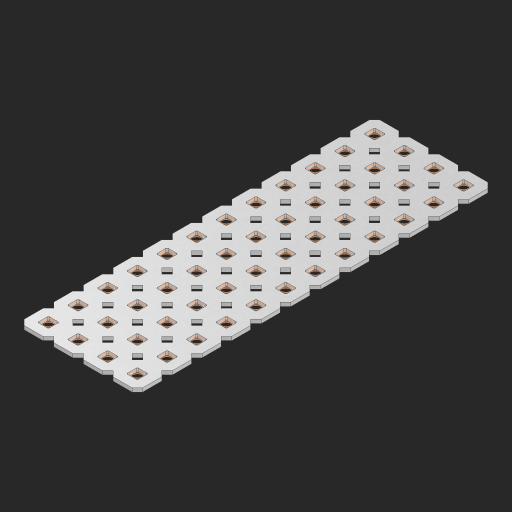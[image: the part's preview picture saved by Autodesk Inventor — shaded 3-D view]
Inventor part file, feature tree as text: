
AUTODESK INVENTOR PART (.ipt)
format: ipt  version: 2023 (Build 270158000, 158)  size: 846,336 bytes
history: native  units: in
note: dims shown in document units (in); Inventor stores cm internally (conversion verified against a paired STEP export)
features: other x49, extrude x47, sketch x2, pattern_linear x1
ambient origin geometry x8: Origin, YZ Plane, XZ Plane, XY Plane, X Axis, Y Axis, Z Axis, Center Point
bodies: Solid1 (feature_tree), Body (feature_tree)
feature tree (99):
  pattern_linear  "Rectangular Pattern1"  Spacing1=0.09in  [1 undecoded]
  sketch  "Sketch1"  dims[d1=0.5in]
  sketch  "Sketch2"  dims[d2=0.182in d3=0.09in d4=0.09in d5=0.09in d6=0.09in d7=0.09in d8=0.09in d9=0.09in d10=0.09in d11=0.02in d13=0.0in d14=0.172in d15=0.0625in d16=0.0in d19=0.5in d22=0.5in]
  other  "Srf1"
  other  "Srf126"
  other  "Srf127"
  other  "Srf128"
  other  "Srf129"
  other  "Srf130"
  other  "Srf131"
  other  "Srf250"
  other  "Srf251"
  other  "Srf252"
  other  "Srf253"
  other  "Srf254"
  other  "Srf268"
  other  "Srf269"
  other  "Srf270"
  other  "Srf271"
  other  "Srf272"
  other  "Srf273"
  other  "Srf274"
  other  "Srf275"
  other  "Srf276"
  other  "Srf277"
  other  "Srf278"
  other  "Srf279"
  other  "Srf293"
  other  "Srf294"
  other  "Srf295"
  other  "Srf296"
  other  "Srf297"
  other  "Srf298"
  other  "Srf299"
  other  "Srf300"
  other  "Srf301"
  other  "Srf302"
  other  "Srf303"
  other  "Srf304"
  other  "Srf318"
  other  "Srf319"
  other  "Srf320"
  other  "Srf321"
  other  "Srf322"
  other  "Srf323"
  other  "Srf324"
  other  "Srf325"
  other  "Srf326"
  other  "Srf327"
  other  "Srf328"
  other  "Srf329"
  other  "Circle"
  extrude  "ExtrusionSrf126"  Depth=0.09in
  extrude  "ExtrusionSrf127"  Depth=0.09in
  extrude  "ExtrusionSrf128"  Depth=0.09in
  extrude  "ExtrusionSrf129"  Depth=0.09in
  extrude  "ExtrusionSrf130"  Depth=0.09in
  extrude  "ExtrusionSrf131"  Depth=0.09in
  extrude  "ExtrusionSrf250"  Depth=0.09in
  extrude  "ExtrusionSrf251"  Depth=0.02in
  extrude  "ExtrusionSrf252"  TaperAngle=0.0deg  [1 undecoded]
  extrude  "ExtrusionSrf253"  Depth=0.5in
  extrude  "ExtrusionSrf254"  Depth=0.0625in TaperAngle=0.0deg
  extrude  "ExtrusionSrf268"  Depth=0.5in
  extrude  "ExtrusionSrf269"  Depth=0.5in
  extrude  "ExtrusionSrf270"  [1 undecoded]
  extrude  "ExtrusionSrf271"  [1 undecoded]
  extrude  "ExtrusionSrf272"  [1 undecoded]
  extrude  "ExtrusionSrf273"  [1 undecoded]
  extrude  "ExtrusionSrf274"  [1 undecoded]
  extrude  "ExtrusionSrf275"  [1 undecoded]
  extrude  "ExtrusionSrf276"  [1 undecoded]
  extrude  "ExtrusionSrf277"  [1 undecoded]
  extrude  "ExtrusionSrf278"  [1 undecoded]
  extrude  "ExtrusionSrf279"  [1 undecoded]
  extrude  "ExtrusionSrf293"  [1 undecoded]
  extrude  "ExtrusionSrf294"  [1 undecoded]
  extrude  "ExtrusionSrf295"  [1 undecoded]
  extrude  "ExtrusionSrf296"  [1 undecoded]
  extrude  "ExtrusionSrf297"  [1 undecoded]
  extrude  "ExtrusionSrf298"  [1 undecoded]
  extrude  "ExtrusionSrf299"  [1 undecoded]
  extrude  "ExtrusionSrf300"  [1 undecoded]
  extrude  "ExtrusionSrf301"  [1 undecoded]
  extrude  "ExtrusionSrf302"  [1 undecoded]
  extrude  "ExtrusionSrf303"  [1 undecoded]
  extrude  "ExtrusionSrf304"  [1 undecoded]
  extrude  "ExtrusionSrf318"  [1 undecoded]
  extrude  "ExtrusionSrf319"  [1 undecoded]
  extrude  "ExtrusionSrf320"  [1 undecoded]
  extrude  "ExtrusionSrf321"  [1 undecoded]
  extrude  "ExtrusionSrf322"  [1 undecoded]
  extrude  "ExtrusionSrf323"  [1 undecoded]
  extrude  "ExtrusionSrf324"  [1 undecoded]
  extrude  "ExtrusionSrf325"  [1 undecoded]
  extrude  "ExtrusionSrf326"  [1 undecoded]
  extrude  "ExtrusionSrf327"  [1 undecoded]
  extrude  "ExtrusionSrf328"  [1 undecoded]
  extrude  "ExtrusionSrf329"  [1 undecoded]
note: 36 required parameter values undecoded (feature->parameter linkage not recoverable at this tier; creation-order binding heuristic only, values carry confidence <= 0.55)
